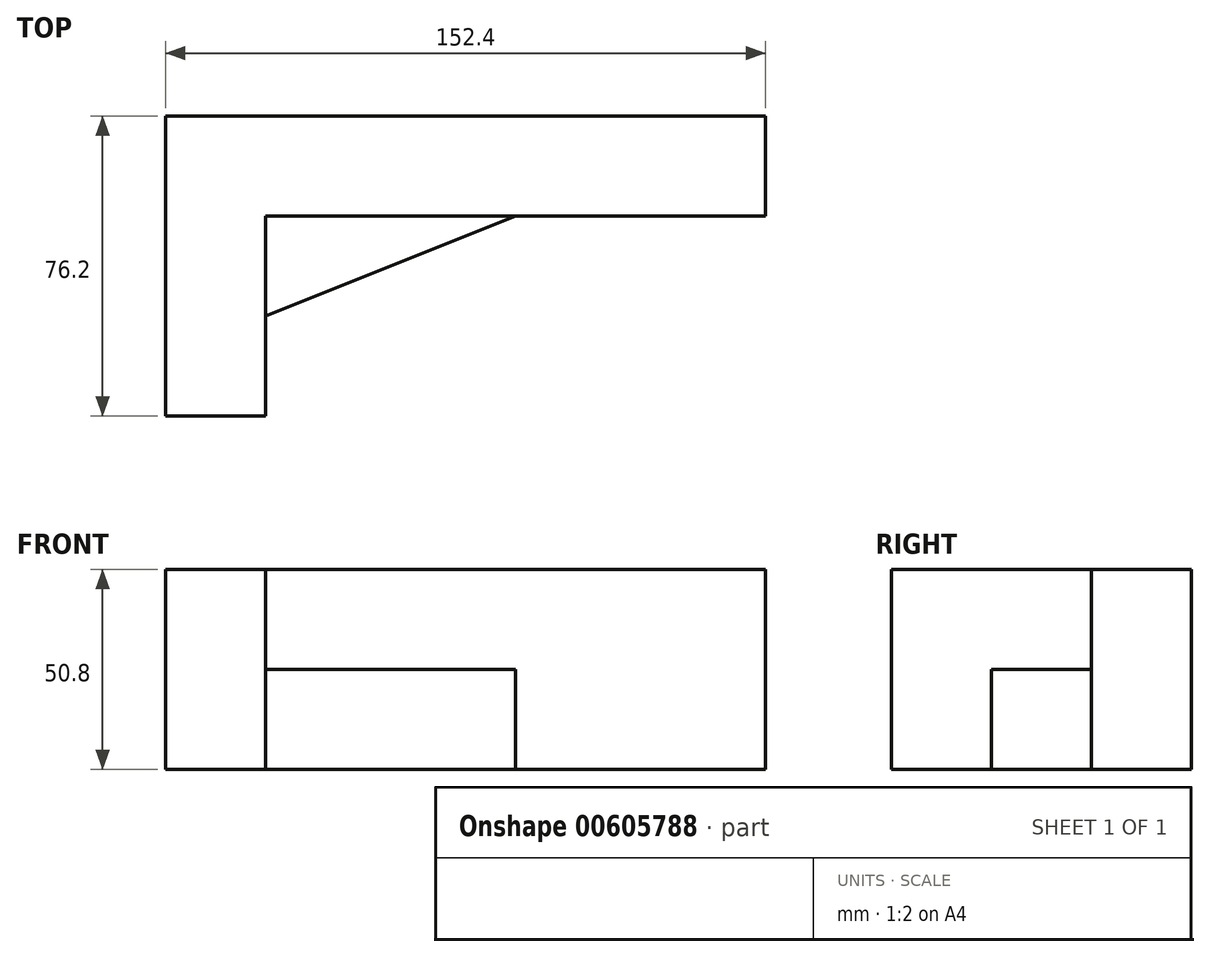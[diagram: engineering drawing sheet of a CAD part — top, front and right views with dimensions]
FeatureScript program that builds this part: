
annotation { "Feature Type Name" : "Feature", "Feature Type Description" : "" }
export const myFeature = defineFeature(function(context is Context, id is Id, definition is map)
    precondition{}
    {
        {
            var Q0;
            Q0=qCreatedBy(makeId("Front.planeOp"),FACE);
            var sketch = newSketch(context, id + "F0", { "sketchPlane" : qUnion([Q0])});
            skLineSegment(sketch, "E0", {"start": v(0, 0) * mm, "end": v(152.4, 0) * mm});
            skLineSegment(sketch, "E1", {"start": v(152.4, 0) * mm, "end": v(152.4, 50.8) * mm});
            skLineSegment(sketch, "E2", {"start": v(152.4, 50.8) * mm, "end": v(0, 50.8) * mm});
            skLineSegment(sketch, "E3", {"start": v(0, 50.8) * mm, "end": v(0, 0) * mm});
            skSolve(sketch);
        }
        {
            var Q0;
            Q0 = qSketchRegion(id + "F0", true);
            extrude(context, id + "F1", {"entities" : qUnion([Q0]), "oppositeDirection" : true, "depth" : 76.2 * mm, "offsetDistance" : 25.4 * mm});
        }
        {
            var Q0;
            Q0=makeQuery(id+"F1.opExtrude","SWEPT_FACE",FACE,{"disambiguationData":[OSD([sQuery(id+"F0.wireOp",EDGE,"E2")])]});
            var sketch = newSketch(context, id + "F2", { "sketchPlane" : qUnion([Q0])});
            skLineSegment(sketch, "E4", {"start": v(0, 0) * mm, "end": v(25.4, 0) * mm});
            skLineSegment(sketch, "E5", {"start": v(25.4, 0) * mm, "end": v(25.4, 50.8) * mm});
            skLineSegment(sketch, "E6", {"start": v(25.4, 50.8) * mm, "end": v(152.4, 50.8) * mm});
            skLineSegment(sketch, "E7", {"start": v(152.4, 50.8) * mm, "end": v(152.4, 0) * mm});
            skLineSegment(sketch, "E8", {"start": v(152.4, 0) * mm, "end": v(25.4, 0) * mm});
            skSolve(sketch);
        }
        {
            var Q0;
            Q0 = qSketchRegion(id + "F2", true);
            extrude(context, id + "F3", {"entities" : qUnion([Q0]), "operationType" : NewBodyOperationType.REMOVE, "oppositeDirection" : true, "depth" : 50.8 * mm, "offsetDistance" : 25.4 * mm});
        }
        {
            var Q0;
            Q0=makeQuery(id+"F1.opExtrude","SWEPT_FACE",FACE,{"disambiguationData":[OSD([sQuery(id+"F0.wireOp",EDGE,"E0")])]});
            var sketch = newSketch(context, id + "F4", { "sketchPlane" : qUnion([Q0])});
            skLineSegment(sketch, "E9", {"start": v(25.4, -50.8) * mm, "end": v(25.4, -25.4) * mm});
            skLineSegment(sketch, "E10", {"start": v(25.4, -25.4) * mm, "end": v(88.9, -50.8) * mm});
            skLineSegment(sketch, "E11", {"start": v(88.9, -50.8) * mm, "end": v(25.4, -50.8) * mm});
            skSolve(sketch);
        }
        {
            var Q0;
            Q0 = qSketchRegion(id + "F4", true);
            extrude(context, id + "F5", {"entities" : qUnion([Q0]), "operationType" : NewBodyOperationType.ADD, "oppositeDirection" : true, "depth" : 25.4 * mm, "offsetDistance" : 25.4 * mm});
        }
    });
